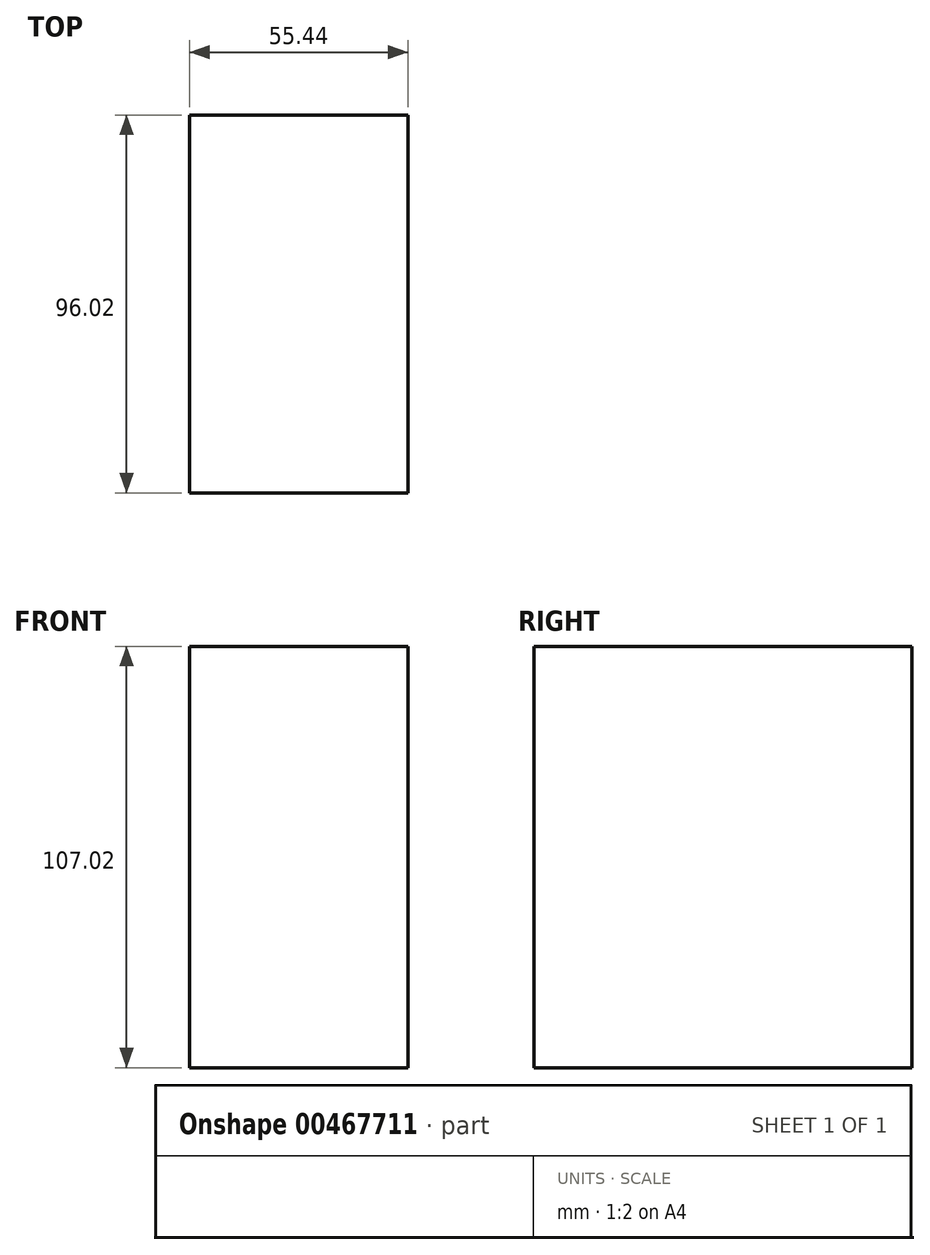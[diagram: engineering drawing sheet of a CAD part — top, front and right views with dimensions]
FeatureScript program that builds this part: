
annotation { "Feature Type Name" : "Feature", "Feature Type Description" : "" }
export const myFeature = defineFeature(function(context is Context, id is Id, definition is map)
    precondition{}
    {
        {
            var Q0;
            Q0=qCreatedBy(makeId("Top.planeOp"),FACE);
            var sketch = newSketch(context, id + "F0", { "sketchPlane" : qUnion([Q0])});
            skCircle(sketch, "E0", {"center": v(-26.56, 5.8) * mm, "radius": 25.4 * mm});
            skSolve(sketch);
        }
        {
            var Q0;
            Q0=qCreatedBy(makeId("Top.planeOp"),FACE);
            var sketch = newSketch(context, id + "F1", { "sketchPlane" : qUnion([Q0])});
            skLineSegment(sketch, "E1.bottom", {"start": v(-43.4, -32.12) * mm, "end": v(12.03, -32.12) * mm});
            skLineSegment(sketch, "E1.top", {"start": v(-43.4, -128.14) * mm, "end": v(12.03, -128.14) * mm});
            skLineSegment(sketch, "E1.left", {"start": v(-43.4, -32.12) * mm, "end": v(-43.4, -128.14) * mm});
            skLineSegment(sketch, "E1.right", {"start": v(12.03, -32.12) * mm, "end": v(12.03, -128.14) * mm});
            skSolve(sketch);
        }
        {
            var Q0;
            Q0=makeQuery(id+"F1.imprint","IMPRINT",FACE,{"disambiguationData":[TD([[makeQuery(id+"F1.imprint","IMPRINT",EDGE,{"derivedFrom":sQuery(id+"F1.wireOp",EDGE,"E1.bottom")}),-1.0]])]});
            extrude(context, id + "F2", {"entities" : qUnion([Q0]), "oppositeDirection" : true, "depth" : 25.4 * mm});
        }
        {
            var Q0;
            Q0 = qSketchRegion(id + "FWx7AkqKyzZBgTk_1", true);
            var Q1;
            Q1=makeQuery(id+"F2.opExtrude","CAP_FACE",FACE,{"disambiguationData":[OSD([sQuery(id+"F1.wireOp",EDGE,"E1.bottom"),sQuery(id+"F1.wireOp",EDGE,"E1.top"),sQuery(id+"F1.wireOp",EDGE,"E1.left"),sQuery(id+"F1.wireOp",EDGE,"E1.right")])],"isStart":true});
            extrude(context, id + "F3", {"entities" : qUnion([Q0, Q1]), "operationType" : NewBodyOperationType.ADD, "depth" : 81.62 * mm});
        }
    });
